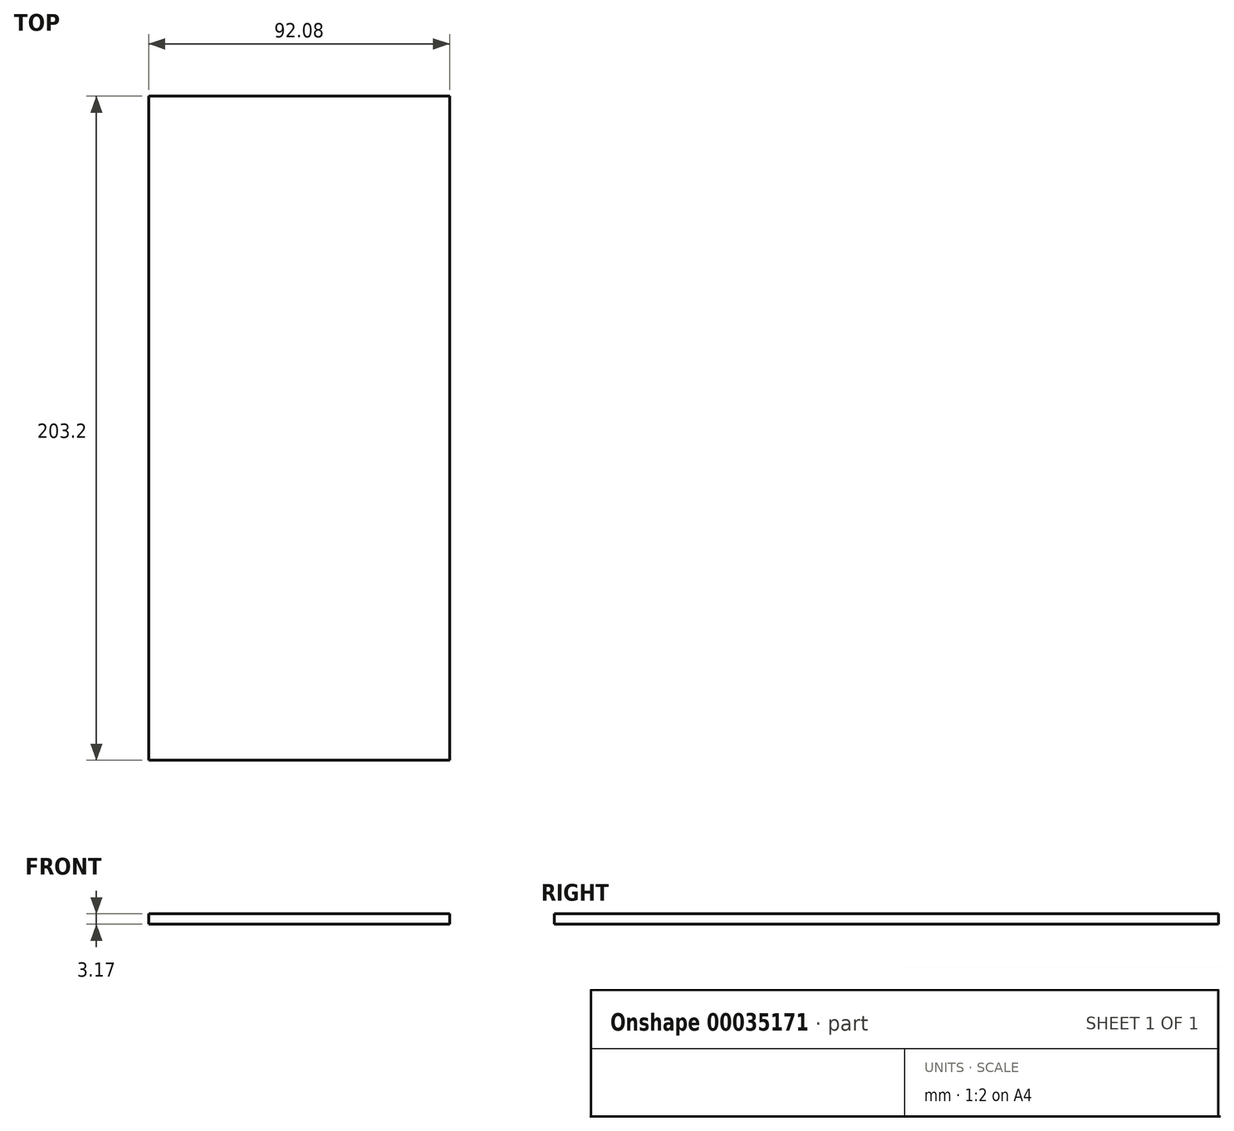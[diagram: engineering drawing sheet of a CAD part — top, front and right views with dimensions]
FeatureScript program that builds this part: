
annotation { "Feature Type Name" : "Feature", "Feature Type Description" : "" }
export const myFeature = defineFeature(function(context is Context, id is Id, definition is map)
    precondition{}
    {
        {
            var Q0;
            Q0=qCreatedBy(makeId("Top.planeOp"),FACE);
            var sketch = newSketch(context, id + "F0", { "sketchPlane" : qUnion([Q0])});
            skLineSegment(sketch, "E0.bottom", {"start": v(-28.87, 109.65) * mm, "end": v(63.2, 109.65) * mm});
            skLineSegment(sketch, "E0.top", {"start": v(-28.87, -93.55) * mm, "end": v(63.2, -93.55) * mm});
            skLineSegment(sketch, "E0.left", {"start": v(-28.87, 109.65) * mm, "end": v(-28.87, -93.55) * mm});
            skLineSegment(sketch, "E0.right", {"start": v(63.2, 109.65) * mm, "end": v(63.2, -93.55) * mm});
            skSolve(sketch);
        }
        {
            var Q0;
            Q0=makeQuery(id+"F0.imprint","IMPRINT",FACE,{"disambiguationData":[TD([[makeQuery(id+"F0.imprint","IMPRINT",EDGE,{"derivedFrom":sQuery(id+"F0.wireOp",EDGE,"E0.bottom")}),-1.0]])]});
            extrude(context, id + "F1", {"entities" : qUnion([Q0]), "depth" : 3.17 * mm});
        }
    });
